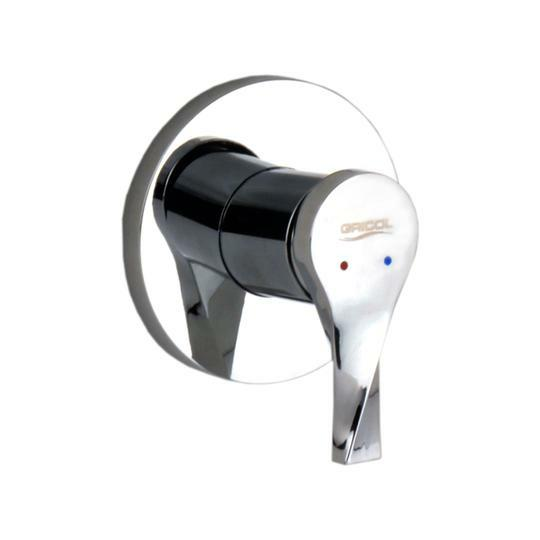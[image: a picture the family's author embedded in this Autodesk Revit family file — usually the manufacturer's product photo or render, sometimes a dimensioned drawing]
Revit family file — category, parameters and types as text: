
# Revit family: 01-2601-11SR DUCHA MONOMANDO SST SIN REGADERA SION
name_source: partatom
category: Plumbing Fixtures
revit_build: Autodesk Revit 2018 (Build: 20170223_1515(x64)
units: mm (PartAtom-declared; Revit-internal decimal feet)

## family parameters
Cut with Voids When Loaded = No
Host = Face
OmniClass Number = 23.31.11.00
Part Type = Normal
Room Calculation Point = No
Round Connector Dimension = Use Diameter
Shared = No

## types (1)
- 01-2601-11SR
    Alto = 72 mm  [stored 0.23622 ft]
    CW Connection = Yes
    Default Elevation = 0 mm  [stored 0 ft]
    Description = Griferia Monomando Ducha
    Diametro = 120 mm
    HW Connection = Yes
    Link Ficha Tecnica = http://infotecnica.gricol.com
    Manufacturer = Gricol
    Metal Laton Cromado = Metal Laton Cromado
    Model = 01-2601-11SR
    Plastico ABS Cromado = Plastico ABS Cromado
    Product Name = DUCHA MONOMANDO SST SIN REGADERA SION
    Profundidad = 72 mm  [stored 0.23622 ft]
    Type Image = DUCHA MONOMANDO SION FOTO.jpg
    URL = https://www.gricol.com
    Vent Connection = No
    Waste Connection = No

note: [stored X ft] marks values corroborated as IEEE doubles in the binary element streams (Revit-internal decimal feet)

## geometry (parser evidence)
native form markers: Blend x2, Sweep x8
no freeform markers — native parametric forms only
